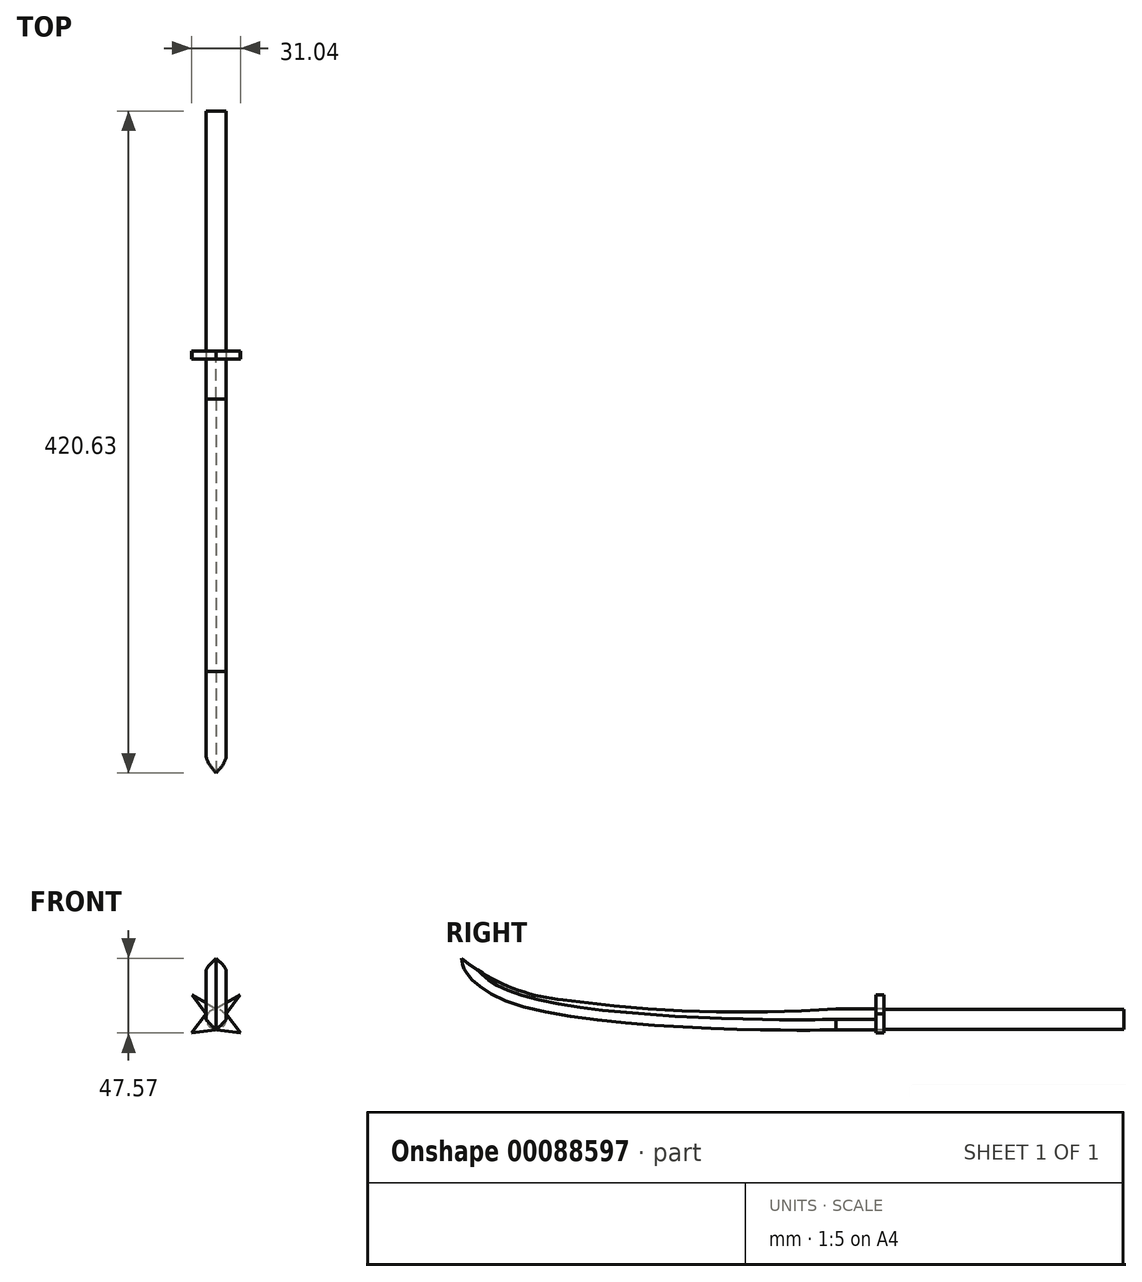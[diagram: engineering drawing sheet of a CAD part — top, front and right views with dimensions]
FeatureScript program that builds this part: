
annotation { "Feature Type Name" : "Feature", "Feature Type Description" : "" }
export const myFeature = defineFeature(function(context is Context, id is Id, definition is map)
    precondition{}
    {
        {
            var Q0;
            Q0=qCreatedBy(makeId("Right.planeOp"),FACE);
            var sketch = newSketch(context, id + "F0", { "sketchPlane" : qUnion([Q0])});
            skFitSpline(sketch, "E0", {"points": [v(-64.62, 32.16) * mm, v(-62.48, 24.54) * mm, v(-33.22, 3.81) * mm, v(142.65, -13.56) * mm, v(173.13, -13.26) * mm], "startDerivative": vector(17.95, -116.7) * mm, "endDerivative": vector(108.77, 1.86) * mm});
            skArc(sketch, "E1", {"start": v(-64.62, 32.16) * mm, "mid": v(-34.32, 13.99) * mm, "end": v(0, 5.64) * mm});
            skArc(sketch, "E2", {"start": v(0, 5.64) * mm, "mid": v(86.42, -1.63) * mm, "end": v(173.13, 0) * mm});
            skLineSegment(sketch, "E3", {"start": v(173.13, 0) * mm, "end": v(173.13, -13.26) * mm});
            skSolve(sketch);
        }
        {
            var Q0;
            Q0 = qSketchRegion(id + "F0", true);
            extrude(context, id + "F1", {"entities" : qUnion([Q0]), "depth" : 12.7 * mm});
        }
        {
            var Q0;
            Q0=makeQuery(id+"F1.opExtrude","SWEPT_FACE",FACE,{"disambiguationData":[OSD([sQuery(id+"F0.wireOp",EDGE,"E3")])]});
            var sketch = newSketch(context, id + "F2", { "sketchPlane" : qUnion([Q0])});
            skLineSegment(sketch, "E4", {"start": v(-12.7, -6.63) * mm, "end": v(-6.35, -13.26) * mm});
            skLineSegment(sketch, "E5", {"start": v(0, -6.63) * mm, "end": v(-6.35, -13.26) * mm});
            skSolve(sketch);
        }
        {
            var Q0;
            {var subQ0=sQuery(id+"F2.wireOp",EDGE,"E4");Q0=makeQuery(id+"F2.imprint","IMPRINT",FACE,{"disambiguationData":[TD([[makeQuery(id+"F2.imprint","IMPRINT",EDGE,{"derivedFrom":subQ0}),-1.0]])]});}
            var Q1;
            {var subQ0=sQuery(id+"F2.wireOp",EDGE,"E5");Q1=makeQuery(id+"F2.imprint","IMPRINT",FACE,{"disambiguationData":[TD([[makeQuery(id+"F2.imprint","IMPRINT",EDGE,{"derivedFrom":subQ0}),1.0]])]});}
            var Q2;
            Q2=makeQuery(id+"F1.opExtrude","CAP_EDGE",EDGE,{"disambiguationData":[OSD([sQuery(id+"F0.wireOp",EDGE,"E0")])],"isStart":false});
            sweep(context, id + "F3", {"operationType" : NewBodyOperationType.REMOVE, "profiles" : qUnion([Q0, Q1]), "path" : qUnion([Q2])});
        }
        {
            var Q0;
            Q0=makeQuery(id+"F1.opExtrude","SWEPT_FACE",FACE,{"disambiguationData":[OSD([sQuery(id+"F0.wireOp",EDGE,"E3")])]});
            extrude(context, id + "F4", {"entities" : qUnion([Q0]), "operationType" : NewBodyOperationType.ADD, "depth" : 25.4 * mm});
        }
        {
            var Q0;
            Q0=makeQuery(id+"F4.opExtrude","CAP_FACE",FACE,{"disambiguationData":[OSD([sQuery(id+"F0.wireOp",EDGE,"E3")])],"isStart":false});
            var sketch = newSketch(context, id + "F5", { "sketchPlane" : qUnion([Q0])});
            skLineSegment(sketch, "E6", {"start": v(-12.7, 0) * mm, "end": v(-21.68, 8.98) * mm});
            skLineSegment(sketch, "E7", {"start": v(0, 0) * mm, "end": v(8.98, 8.98) * mm});
            skLineSegment(sketch, "E8", {"start": v(0, -6.63) * mm, "end": v(9.17, -15.41) * mm});
            skLineSegment(sketch, "E9", {"start": v(-12.7, -6.63) * mm, "end": v(-21.87, -15.41) * mm});
            skLineSegment(sketch, "E10", {"start": v(-21.68, 8.98) * mm, "end": v(-6.35, 0) * mm});
            skLineSegment(sketch, "E11", {"start": v(8.98, 8.98) * mm, "end": v(-6.35, 0) * mm});
            skLineSegment(sketch, "E12", {"start": v(-21.87, -15.41) * mm, "end": v(-6.35, -13.26) * mm});
            skLineSegment(sketch, "E13", {"start": v(9.17, -15.41) * mm, "end": v(-6.35, -13.26) * mm});
            skLineSegment(sketch, "E14", {"start": v(-21.68, 8.98) * mm, "end": v(-12.7, -3.31) * mm});
            skLineSegment(sketch, "E15", {"start": v(-12.7, -3.31) * mm, "end": v(-21.87, -15.41) * mm});
            skLineSegment(sketch, "E16", {"start": v(8.98, 8.98) * mm, "end": v(0, -3.31) * mm});
            skLineSegment(sketch, "E17", {"start": v(0, -3.31) * mm, "end": v(9.17, -15.41) * mm});
            skSolve(sketch);
        }
        {
            var Q0;
            Q0 = qSketchRegion(id + "F5", true);
            extrude(context, id + "F6", {"entities" : qUnion([Q0]), "depth" : 5.08 * mm});
        }
        {
            var Q0;
            Q0=makeQuery(id+"F6.opExtrude","CAP_FACE",FACE,{"disambiguationData":[OSD([sQuery(id+"F5.wireOp",EDGE,"E10"),sQuery(id+"F5.wireOp",EDGE,"E11"),sQuery(id+"F5.wireOp",EDGE,"E12"),sQuery(id+"F5.wireOp",EDGE,"E13"),sQuery(id+"F5.wireOp",EDGE,"E14"),sQuery(id+"F5.wireOp",EDGE,"E15"),sQuery(id+"F5.wireOp",EDGE,"E16"),sQuery(id+"F5.wireOp",EDGE,"E17")])],"isStart":false});
            var sketch = newSketch(context, id + "F7", { "sketchPlane" : qUnion([Q0])});
            skLineSegment(sketch, "E18", {"start": v(-6.35, 0) * mm, "end": v(-6.35, -13.26) * mm});
            skCircle(sketch, "E19", {"center": v(-6.35, -6.63) * mm, "radius": 6.35 * mm});
            skSolve(sketch);
        }
        {
            var Q0;
            Q0 = qSketchRegion(id + "F7", true);
            extrude(context, id + "F8", {"entities" : qUnion([Q0]), "operationType" : NewBodyOperationType.ADD, "depth" : 152.4 * mm});
        }
    });
